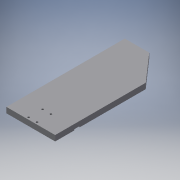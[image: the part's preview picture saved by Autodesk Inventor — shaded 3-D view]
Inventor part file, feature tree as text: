
AUTODESK INVENTOR PART (.ipt)
format: ipt  version: 2018 (Build 220112000, 112)  size: 119,808 bytes
history: native  units: mm
features: sketch x3, extrude x2, other x1, hole x1
ambient origin geometry x8: Origin, YZ Plane, XZ Plane, XY Plane, X Axis, Y Axis, Z Axis, Center Point
bodies: Body1 (feature_tree)
feature tree (7):
  other  "Sólido1"
  extrude  "Extrusão1"  Depth=340.0mm
  extrude  "Extrusão3"  Depth=260.0mm
  hole  "Furo1"  [1 undecoded]
  sketch  "Esboço1"  dims[d0=140.0mm d1=340.0mm]
  sketch  "Esboço3"  dims[d2=70.0mm d3=260.0mm]
  sketch  "Esboço4"  dims[d4=15.88mm d5=0.0mm d11=15.98mm d12=3.0mm d13=0.0mm d14=5.5mm d15=6.0mm d16=8.0mm d17=6.0mm d18=90.0deg d19=8.0mm d20=20.594885mm]
note: 1 required parameter value undecoded (feature->parameter linkage not recoverable at this tier; creation-order binding heuristic only, values carry confidence <= 0.55)
